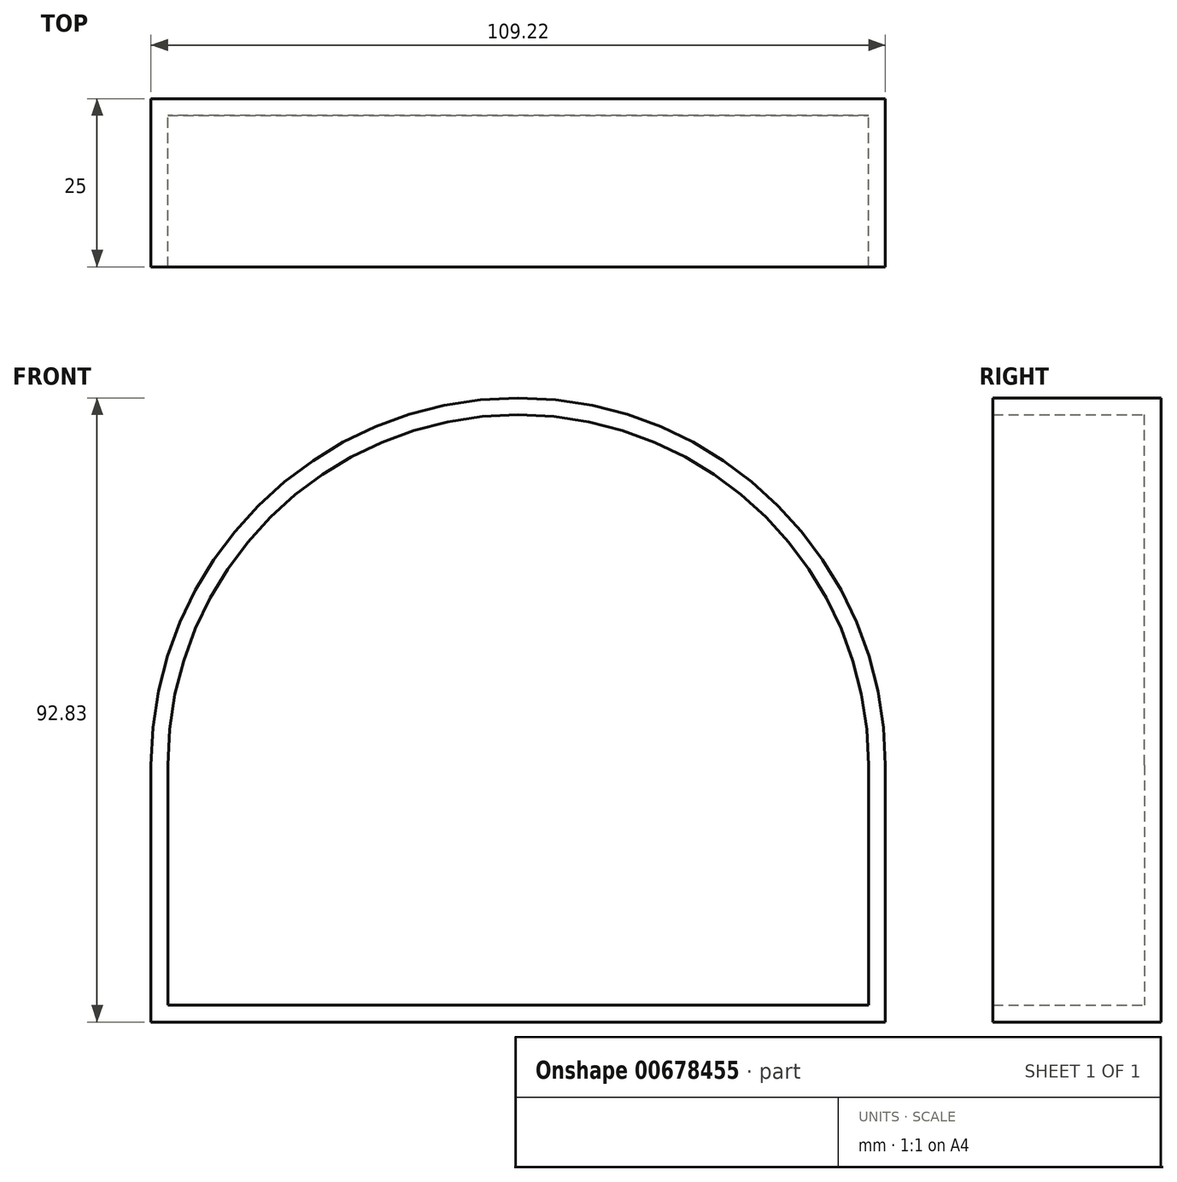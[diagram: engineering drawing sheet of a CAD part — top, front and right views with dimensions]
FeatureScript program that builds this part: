
annotation { "Feature Type Name" : "Feature", "Feature Type Description" : "" }
export const myFeature = defineFeature(function(context is Context, id is Id, definition is map)
    precondition{}
    {
        {
            var Q0;
            Q0=qCreatedBy(makeId("Front.planeOp"),FACE);
            var sketch = newSketch(context, id + "F0", { "sketchPlane" : qUnion([Q0])});
            skLineSegment(sketch, "E0", {"start": v(-58.49, -2.16) * mm, "end": v(-58.49, -40.38) * mm});
            skLineSegment(sketch, "E1", {"start": v(-58.49, -40.38) * mm, "end": v(50.73, -40.38) * mm});
            skLineSegment(sketch, "E2", {"start": v(50.73, -40.38) * mm, "end": v(50.73, -2.16) * mm});
            skArc(sketch, "E3", {"start": v(50.73, -2.16) * mm, "mid": v(-3.88, 52.45) * mm, "end": v(-58.49, -2.16) * mm});
            skSolve(sketch);
        }
        {
            var Q0;
            Q0=makeQuery(id+"F0.imprint","IMPRINT",FACE,{"disambiguationData":[TD([[makeQuery(id+"F0.imprint","IMPRINT",EDGE,{"derivedFrom":sQuery(id+"F0.wireOp",EDGE,"E0")}),1.0]])]});
            extrude(context, id + "F1", {"entities" : qUnion([Q0]), "depth" : 25 * mm, "offsetDistance" : 25 * mm});
        }
        {
            var Q0;
            Q0=makeQuery(id+"F1.opExtrude","CAP_FACE",FACE,{"disambiguationData":[OSD([sQuery(id+"F0.wireOp",EDGE,"E0"),sQuery(id+"F0.wireOp",EDGE,"E1"),sQuery(id+"F0.wireOp",EDGE,"E2"),sQuery(id+"F0.wireOp",EDGE,"E3")])],"isStart":false});
            shell(context, id + "F2", {"entities" : qUnion([Q0]), "thickness" : 2.5 * mm});
        }
    });
